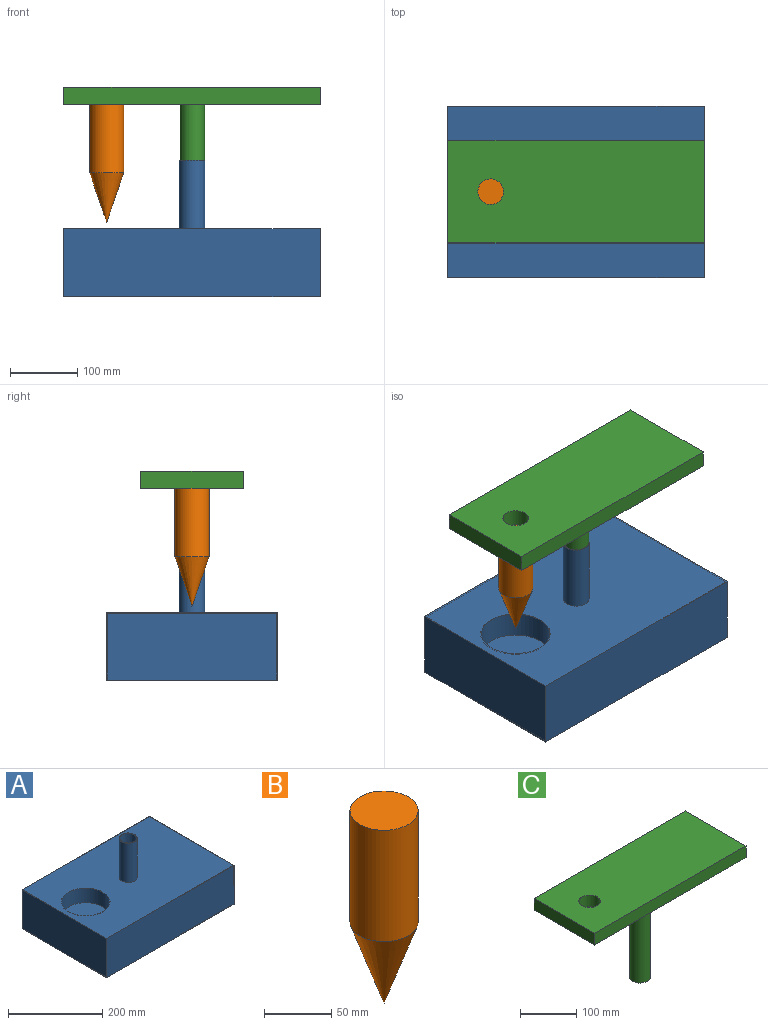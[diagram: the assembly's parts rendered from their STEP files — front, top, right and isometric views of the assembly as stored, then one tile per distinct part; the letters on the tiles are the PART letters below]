
ASSEMBLY  parts=3 mates=2
PART A: 19 faces, bbox 381x254x203.2 mm
  f0: plane 381x101.6mm, normal (0,1,0), area 38709.6mm2, adj f1,f3,f4,f5
  f1: plane 254x101.6mm, normal (-1,0,0), area 25806.4mm2, adj f0,f2,f4,f5
  f2: plane 381x101.6mm, normal (0,-1,0), area 38709.6mm2, adj f1,f3,f4,f5
  f3: plane 254x101.6mm, normal (1,0,0), area 25806.4mm2, adj f0,f2,f4,f5
  f4: plane 381x254mm, normal (0,0,1), area 87526.6mm2, adj f0,f1,f2,f3,f6,f8
  f5: plane 381x254mm, normal (0,0,-1), area 96774mm2, adj f0,f1,f2,f3
  f6: cylinder r=50.8mm len=101.6mm, axis (0,0,1), area 12161mm2, adj f4,f7
  f7: plane 101.6x101.6mm, normal (0,0,1), area 8107.3mm2, adj f6
  f8: cylinder r=19.05mm len=101.6mm, axis (0,0,-1), area 12161mm2, adj f4,f9
  f9: plane 38.1x38.1mm, normal (0,0,1), area 146.9mm2, adj f8,f18
  f10: plane 378.46x99.06mm, normal (0,-1,0), area 37490.2mm2, adj f11,f13,f14,f15
  f11: plane 251.46x99.06mm, normal (1,0,0), area 24909.6mm2, adj f10,f12,f14,f15
  f12: plane 378.46x99.06mm, normal (0,1,0), area 37490.2mm2, adj f11,f13,f14,f15
  f13: plane 251.46x99.06mm, normal (-1,0,0), area 24909.6mm2, adj f10,f12,f14,f15
  f14: plane 378.46x251.46mm, normal (0,0,-1), area 85656.7mm2, adj f10,f11,f12,f13,f16,f18
  f15: plane 378.46x251.46mm, normal (0,0,1), area 95167.6mm2, adj f10,f11,f12,f13
  f16: cylinder r=52.07mm len=104.14mm, axis (0,0,1), area 12465mm2, adj f14,f17
  f17: plane 104.14x104.14mm, normal (0,0,-1), area 8517.8mm2, adj f16
  f18: cylinder r=17.78mm len=102.87mm, axis (0,0,-1), area 11492.1mm2, adj f9,f14
PART B: 4 faces, bbox 50.8x50.8x175.6 mm
  f0: cylinder r=25.4mm len=101.6mm, axis (0,0,-1), area 16214.6mm2, adj f1,f2
  f1: plane 50.8x50.8mm, normal (0,0,1), area 2026.8mm2, adj f0
  f2: plane 50.8x50.8mm, normal (0,0,-1), area 3.5mm2, adj f0,f3
  f3: cone r=0mm half-angle=18.9deg, axis (0,0,1), area 6233.5mm2, adj f2
PART C: 9 faces, bbox 381x152.4x228.6 mm
  f0: cylinder r=18.41mm len=203.2mm, axis (0,0,-1), area 23511.2mm2, adj f1,f8
  f1: plane 36.83x36.83mm, normal (0,0,-1), area 1065.4mm2, adj f0
  f2: plane 381x25.4mm, normal (0,1,0), area 9677.4mm2, adj f3,f6,f7,f8
  f3: plane 152.4x25.4mm, normal (-1,0,0), area 3871mm2, adj f2,f4,f7,f8
  f4: plane 381x25.4mm, normal (0,-1,0), area 9677.4mm2, adj f3,f6,f7,f8
  f5: cylinder r=19.05mm len=38.1mm, axis (0,0,-1), area 3040.2mm2, adj f7,f8
  f6: plane 152.4x25.4mm, normal (1,0,0), area 3871mm2, adj f2,f4,f7,f8
  f7: plane 381x152.4mm, normal (0,0,1), area 56924.3mm2, adj f2,f3,f4,f5,f6
  f8: plane 381x152.4mm, normal (0,0,-1), area 55859mm2, adj f0,f2,f3,f4,f5,f6
PLACE A t=(-76.32,31.4,-64.59)mm fixed
PLACE B t=(-202.89,31.4,120.14)mm
PLACE C t=(-75.89,31.4,18.54)mm
MATE slider C.f0 <-> A.f8  axis (0,0,-1) through (-75.89,31.4,18.54)mm
MATE fastened C.f5 <-> B.f0  axis (0,0,-1) through (-202.89,31.4,221.74)mm
